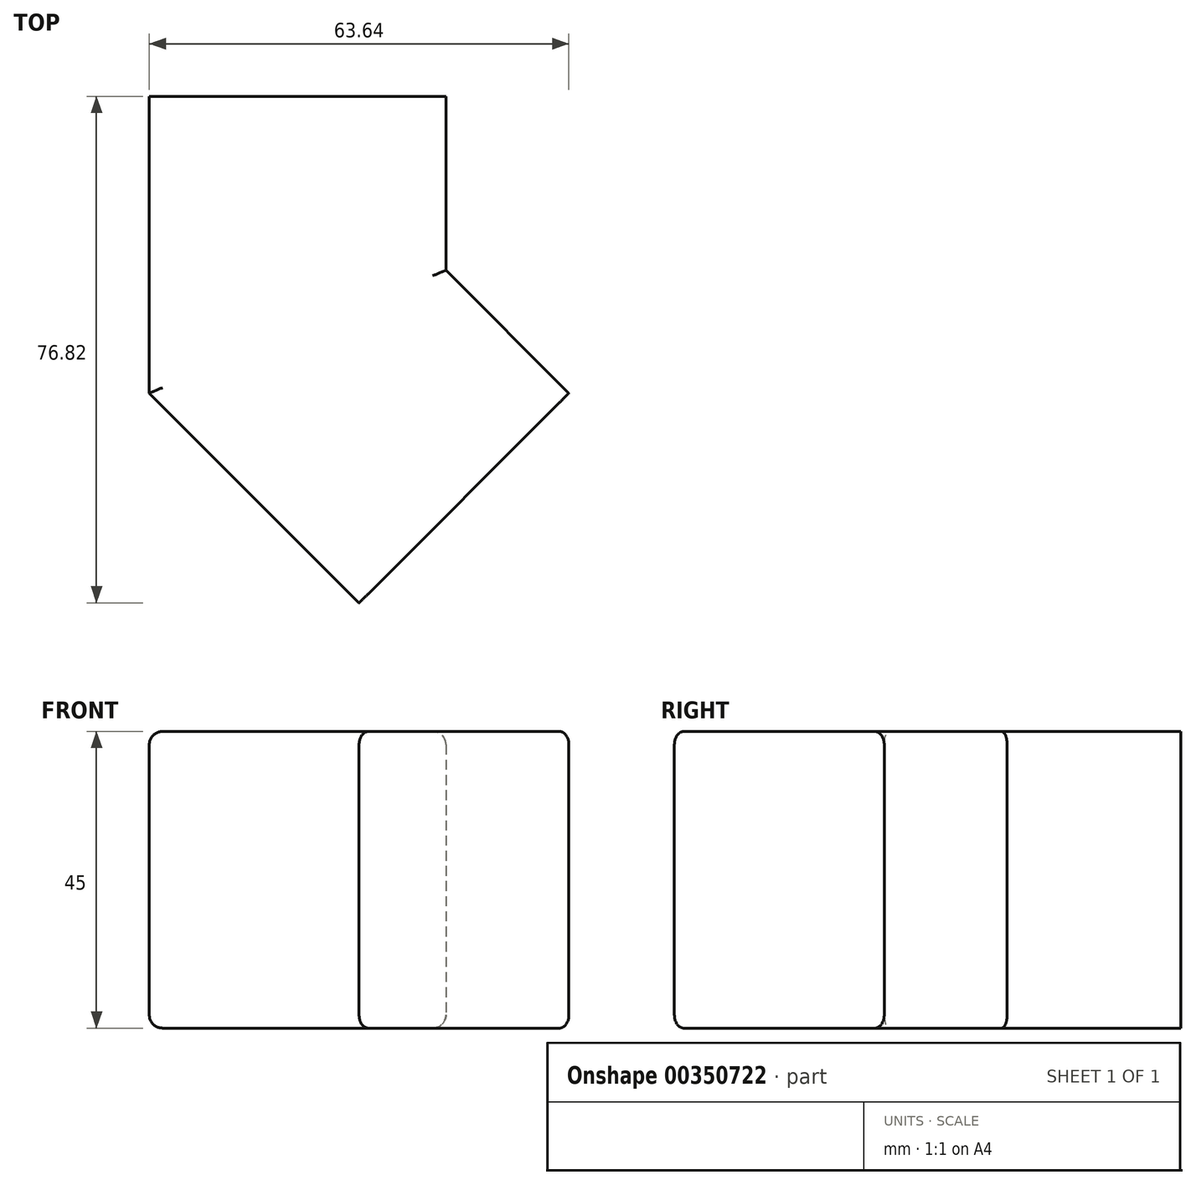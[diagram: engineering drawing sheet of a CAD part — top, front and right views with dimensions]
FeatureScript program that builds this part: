
annotation { "Feature Type Name" : "Feature", "Feature Type Description" : "" }
export const myFeature = defineFeature(function(context is Context, id is Id, definition is map)
    precondition{}
    {
        {
            var Q0;
            Q0=qCreatedBy(makeId("Top.planeOp"),FACE);
            var sketch = newSketch(context, id + "F0", { "sketchPlane" : qUnion([Q0])});
            skLineSegment(sketch, "E0", {"start": v(0, 0) * mm, "end": v(0, 45) * mm});
            skLineSegment(sketch, "E1", {"start": v(0, 45) * mm, "end": v(45, 45) * mm});
            skLineSegment(sketch, "E2", {"start": v(45, 45) * mm, "end": v(45, 18.64) * mm});
            skLineSegment(sketch, "E3", {"start": v(0, 0) * mm, "end": v(31.82, -31.82) * mm});
            skLineSegment(sketch, "E4", {"start": v(31.82, -31.82) * mm, "end": v(63.64, 0) * mm});
            skLineSegment(sketch, "E5", {"start": v(63.64, 0) * mm, "end": v(45, 18.64) * mm});
            skSolve(sketch);
        }
        {
            var Q0;
            Q0 = qSketchRegion(id + "F0", true);
            extrude(context, id + "F1", {"entities" : qUnion([Q0]), "depth" : 45 * mm});
        }
        {
            var Q0;
            Q0=makeQuery(id+"F1.opExtrude","CAP_EDGE",EDGE,{"disambiguationData":[OSD([sQuery(id+"F0.wireOp",EDGE,"E5")])],"isStart":true});
            var Q1;
            Q1=makeQuery(id+"F1.opExtrude","CAP_EDGE",EDGE,{"disambiguationData":[OSD([sQuery(id+"F0.wireOp",EDGE,"E2")])],"isStart":true});
            var Q2;
            Q2=makeQuery(id+"F1.opExtrude","CAP_EDGE",EDGE,{"disambiguationData":[OSD([sQuery(id+"F0.wireOp",EDGE,"E3")])],"isStart":true});
            var Q3;
            Q3=makeQuery(id+"F1.opExtrude","CAP_EDGE",EDGE,{"disambiguationData":[OSD([sQuery(id+"F0.wireOp",EDGE,"E0")])],"isStart":true});
            var Q4;
            Q4=makeQuery(id+"F1.opExtrude","CAP_EDGE",EDGE,{"disambiguationData":[OSD([sQuery(id+"F0.wireOp",EDGE,"E5")])],"isStart":false});
            var Q5;
            Q5=makeQuery(id+"F1.opExtrude","CAP_EDGE",EDGE,{"disambiguationData":[OSD([sQuery(id+"F0.wireOp",EDGE,"E2")])],"isStart":false});
            var Q6;
            Q6=makeQuery(id+"F1.opExtrude","CAP_EDGE",EDGE,{"disambiguationData":[OSD([sQuery(id+"F0.wireOp",EDGE,"E0")])],"isStart":false});
            var Q7;
            Q7=makeQuery(id+"F1.opExtrude","CAP_EDGE",EDGE,{"disambiguationData":[OSD([sQuery(id+"F0.wireOp",EDGE,"E3")])],"isStart":false});
            fillet(context, id + "F2", {"entities" : qUnion([Q0, Q1, Q2, Q3, Q4, Q5, Q6, Q7]), "radius" : 2 * mm, "tangentPropagation" : true, "allowEdgeOverflow" : false});
        }
    });
